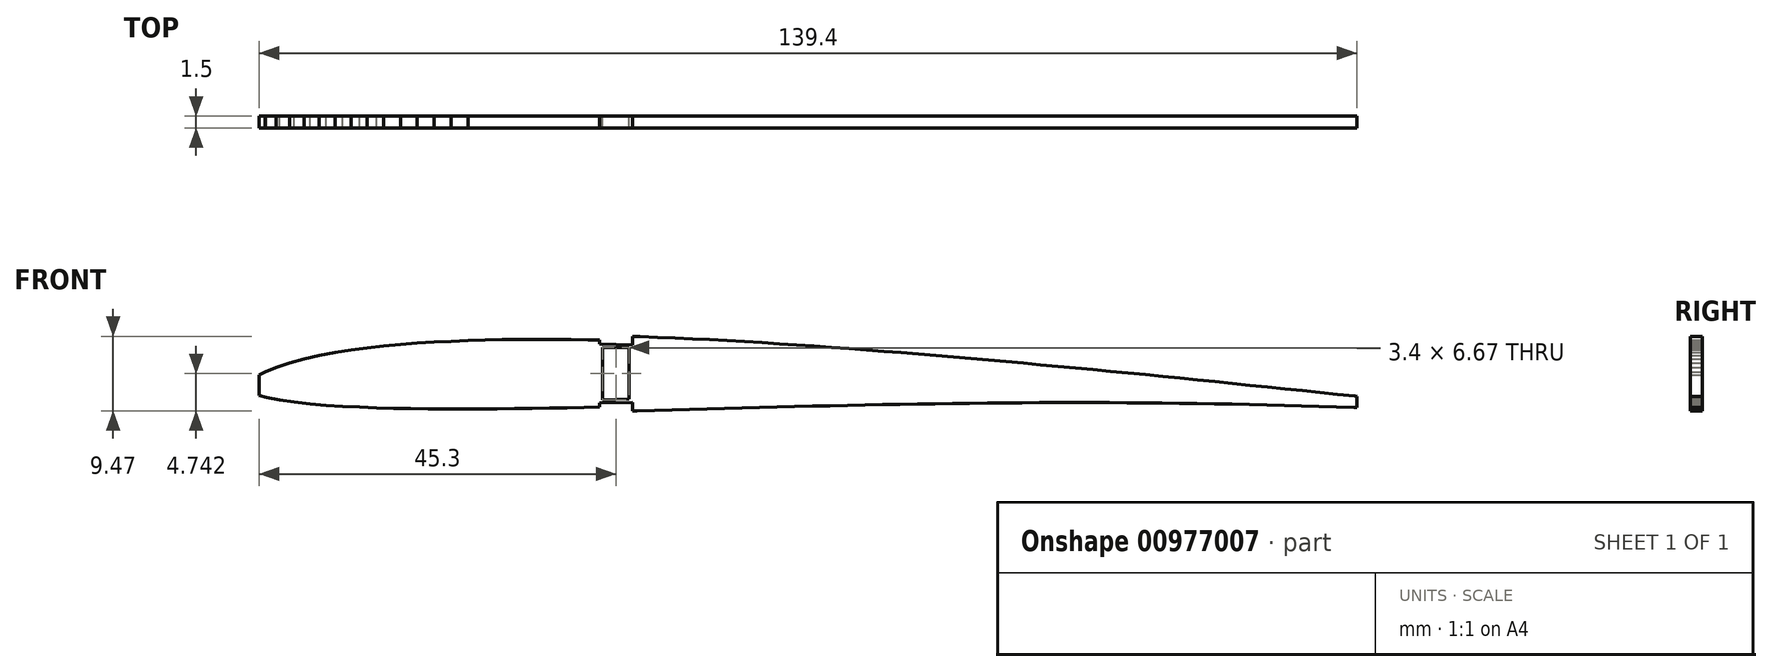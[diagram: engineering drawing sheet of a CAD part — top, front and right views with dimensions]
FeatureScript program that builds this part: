
annotation { "Feature Type Name" : "Feature", "Feature Type Description" : "" }
export const myFeature = defineFeature(function(context is Context, id is Id, definition is map)
    precondition{}
    {
        {
            var Q0;
            Q0=qCreatedBy(makeId("Front.planeOp"),FACE);
            var sketch = newSketch(context, id + "F0", { "sketchPlane" : qUnion([Q0])});
            skLineSegment(sketch, "E0", {"start": v(142, 2.16) * mm, "end": v(141.76, 2.2) * mm});
            skLineSegment(sketch, "E1", {"start": v(141.76, 2.2) * mm, "end": v(139.54, 2.42) * mm});
            skLineSegment(sketch, "E2", {"start": v(139.54, 2.42) * mm, "end": v(137.32, 2.66) * mm});
            skLineSegment(sketch, "E3", {"start": v(137.32, 2.66) * mm, "end": v(135.1, 2.89) * mm});
            skLineSegment(sketch, "E4", {"start": v(135.1, 2.89) * mm, "end": v(132.89, 3.12) * mm});
            skLineSegment(sketch, "E5", {"start": v(132.89, 3.12) * mm, "end": v(130.67, 3.35) * mm});
            skLineSegment(sketch, "E6", {"start": v(130.67, 3.35) * mm, "end": v(128.45, 3.57) * mm});
            skLineSegment(sketch, "E7", {"start": v(128.45, 3.57) * mm, "end": v(126.23, 3.8) * mm});
            skLineSegment(sketch, "E8", {"start": v(126.23, 3.8) * mm, "end": v(124.02, 4.03) * mm});
            skLineSegment(sketch, "E9", {"start": v(124.02, 4.03) * mm, "end": v(121.8, 4.25) * mm});
            skLineSegment(sketch, "E10", {"start": v(121.8, 4.25) * mm, "end": v(119.58, 4.47) * mm});
            skLineSegment(sketch, "E11", {"start": v(119.58, 4.47) * mm, "end": v(117.37, 4.7) * mm});
            skLineSegment(sketch, "E12", {"start": v(117.37, 4.7) * mm, "end": v(115.15, 4.91) * mm});
            skLineSegment(sketch, "E13", {"start": v(115.15, 4.91) * mm, "end": v(112.94, 5.13) * mm});
            skLineSegment(sketch, "E14", {"start": v(112.94, 5.13) * mm, "end": v(110.72, 5.34) * mm});
            skLineSegment(sketch, "E15", {"start": v(110.72, 5.34) * mm, "end": v(108.5, 5.56) * mm});
            skLineSegment(sketch, "E16", {"start": v(108.5, 5.56) * mm, "end": v(106.29, 5.77) * mm});
            skLineSegment(sketch, "E17", {"start": v(106.29, 5.77) * mm, "end": v(104.07, 5.98) * mm});
            skLineSegment(sketch, "E18", {"start": v(104.07, 5.98) * mm, "end": v(101.86, 6.18) * mm});
            skLineSegment(sketch, "E19", {"start": v(101.86, 6.18) * mm, "end": v(99.64, 6.38) * mm});
            skLineSegment(sketch, "E20", {"start": v(99.64, 6.38) * mm, "end": v(97.43, 6.58) * mm});
            skLineSegment(sketch, "E21", {"start": v(97.43, 6.58) * mm, "end": v(95.22, 6.78) * mm});
            skLineSegment(sketch, "E22", {"start": v(95.22, 6.78) * mm, "end": v(93, 6.98) * mm});
            skLineSegment(sketch, "E23", {"start": v(93, 6.98) * mm, "end": v(90.79, 7.17) * mm});
            skLineSegment(sketch, "E24", {"start": v(90.79, 7.17) * mm, "end": v(88.57, 7.35) * mm});
            skLineSegment(sketch, "E25", {"start": v(88.57, 7.35) * mm, "end": v(86.36, 7.54) * mm});
            skLineSegment(sketch, "E26", {"start": v(86.36, 7.54) * mm, "end": v(84.14, 7.72) * mm});
            skLineSegment(sketch, "E27", {"start": v(84.14, 7.72) * mm, "end": v(81.93, 7.9) * mm});
            skLineSegment(sketch, "E28", {"start": v(81.93, 7.9) * mm, "end": v(79.72, 8.06) * mm});
            skLineSegment(sketch, "E29", {"start": v(79.72, 8.06) * mm, "end": v(77.5, 8.23) * mm});
            skLineSegment(sketch, "E30", {"start": v(77.5, 8.23) * mm, "end": v(75.3, 8.4) * mm});
            skLineSegment(sketch, "E31", {"start": v(75.3, 8.4) * mm, "end": v(73.08, 8.55) * mm});
            skLineSegment(sketch, "E32", {"start": v(73.08, 8.55) * mm, "end": v(70.87, 8.7) * mm});
            skLineSegment(sketch, "E33", {"start": v(70.87, 8.7) * mm, "end": v(68.66, 8.85) * mm});
            skLineSegment(sketch, "E34", {"start": v(68.66, 8.85) * mm, "end": v(66.45, 8.98) * mm});
            skLineSegment(sketch, "E35", {"start": v(66.45, 8.98) * mm, "end": v(64.24, 9.12) * mm});
            skLineSegment(sketch, "E36", {"start": v(64.24, 9.12) * mm, "end": v(62.03, 9.24) * mm});
            skLineSegment(sketch, "E37", {"start": v(62.03, 9.24) * mm, "end": v(59.82, 9.36) * mm});
            skLineSegment(sketch, "E38", {"start": v(59.82, 9.36) * mm, "end": v(57.61, 9.47) * mm});
            skLineSegment(sketch, "E39", {"start": v(57.61, 9.47) * mm, "end": v(55.4, 9.57) * mm});
            skLineSegment(sketch, "E40", {"start": v(55.4, 9.57) * mm, "end": v(53.2, 9.66) * mm});
            skLineSegment(sketch, "E41", {"start": v(53.2, 9.66) * mm, "end": v(51, 9.74) * mm});
            skLineSegment(sketch, "E42", {"start": v(51, 9.74) * mm, "end": v(50, 9.78) * mm});
            skLineSegment(sketch, "E43", {"start": v(45.8, 9.3) * mm, "end": v(44.39, 9.33) * mm});
            skLineSegment(sketch, "E44", {"start": v(44.39, 9.33) * mm, "end": v(42.2, 9.36) * mm});
            skLineSegment(sketch, "E45", {"start": v(42.2, 9.36) * mm, "end": v(40, 9.39) * mm});
            skLineSegment(sketch, "E46", {"start": v(40, 9.39) * mm, "end": v(37.82, 9.4) * mm});
            skLineSegment(sketch, "E47", {"start": v(37.82, 9.4) * mm, "end": v(35.64, 9.39) * mm});
            skLineSegment(sketch, "E48", {"start": v(35.64, 9.39) * mm, "end": v(33.46, 9.36) * mm});
            skLineSegment(sketch, "E49", {"start": v(33.46, 9.36) * mm, "end": v(31.29, 9.32) * mm});
            skLineSegment(sketch, "E50", {"start": v(31.29, 9.32) * mm, "end": v(29.12, 9.25) * mm});
            skLineSegment(sketch, "E51", {"start": v(29.12, 9.25) * mm, "end": v(26.96, 9.16) * mm});
            skLineSegment(sketch, "E52", {"start": v(26.96, 9.16) * mm, "end": v(24.8, 9.05) * mm});
            skLineSegment(sketch, "E53", {"start": v(24.8, 9.05) * mm, "end": v(22.67, 8.92) * mm});
            skLineSegment(sketch, "E54", {"start": v(22.67, 8.92) * mm, "end": v(20.54, 8.75) * mm});
            skLineSegment(sketch, "E55", {"start": v(20.54, 8.75) * mm, "end": v(18.42, 8.55) * mm});
            skLineSegment(sketch, "E56", {"start": v(18.42, 8.55) * mm, "end": v(16.33, 8.32) * mm});
            skLineSegment(sketch, "E57", {"start": v(16.33, 8.32) * mm, "end": v(14.26, 8.04) * mm});
            skLineSegment(sketch, "E58", {"start": v(14.26, 8.04) * mm, "end": v(12.22, 7.72) * mm});
            skLineSegment(sketch, "E59", {"start": v(12.22, 7.72) * mm, "end": v(10.23, 7.35) * mm});
            skLineSegment(sketch, "E60", {"start": v(10.23, 7.35) * mm, "end": v(8.3, 6.91) * mm});
            skLineSegment(sketch, "E61", {"start": v(8.3, 6.91) * mm, "end": v(6.46, 6.42) * mm});
            skLineSegment(sketch, "E62", {"start": v(6.46, 6.42) * mm, "end": v(4.77, 5.86) * mm});
            skLineSegment(sketch, "E63", {"start": v(4.77, 5.86) * mm, "end": v(3.34, 5.26) * mm});
            skLineSegment(sketch, "E64", {"start": v(3.34, 5.26) * mm, "end": v(2.6, 4.87) * mm});
            skLineSegment(sketch, "E65", {"start": v(50, 9.78) * mm, "end": v(50, 9.18) * mm});
            skLineSegment(sketch, "E66", {"start": v(142, 0.74) * mm, "end": v(142, 2.16) * mm});
            skLineSegment(sketch, "E67", {"start": v(2.6, 2.28) * mm, "end": v(2.6, 4.87) * mm});
            skLineSegment(sketch, "E68", {"start": v(2.6, 2.28) * mm, "end": v(3.55, 2.03) * mm});
            skLineSegment(sketch, "E69", {"start": v(3.55, 2.03) * mm, "end": v(5.16, 1.7) * mm});
            skLineSegment(sketch, "E70", {"start": v(5.16, 1.7) * mm, "end": v(7.04, 1.43) * mm});
            skLineSegment(sketch, "E71", {"start": v(7.04, 1.43) * mm, "end": v(9.04, 1.2) * mm});
            skLineSegment(sketch, "E72", {"start": v(9.04, 1.2) * mm, "end": v(11.11, 1.03) * mm});
            skLineSegment(sketch, "E73", {"start": v(11.11, 1.03) * mm, "end": v(13.22, 0.9) * mm});
            skLineSegment(sketch, "E74", {"start": v(13.22, 0.9) * mm, "end": v(15.35, 0.79) * mm});
            skLineSegment(sketch, "E75", {"start": v(15.35, 0.79) * mm, "end": v(17.5, 0.7) * mm});
            skLineSegment(sketch, "E76", {"start": v(17.5, 0.7) * mm, "end": v(19.68, 0.64) * mm});
            skLineSegment(sketch, "E77", {"start": v(19.68, 0.64) * mm, "end": v(21.86, 0.6) * mm});
            skLineSegment(sketch, "E78", {"start": v(21.86, 0.6) * mm, "end": v(24.04, 0.57) * mm});
            skLineSegment(sketch, "E79", {"start": v(24.04, 0.57) * mm, "end": v(26.23, 0.56) * mm});
            skLineSegment(sketch, "E80", {"start": v(26.23, 0.56) * mm, "end": v(28.43, 0.56) * mm});
            skLineSegment(sketch, "E81", {"start": v(28.43, 0.56) * mm, "end": v(30.63, 0.56) * mm});
            skLineSegment(sketch, "E82", {"start": v(30.63, 0.56) * mm, "end": v(32.83, 0.58) * mm});
            skLineSegment(sketch, "E83", {"start": v(32.83, 0.58) * mm, "end": v(35.04, 0.6) * mm});
            skLineSegment(sketch, "E84", {"start": v(35.04, 0.6) * mm, "end": v(37.25, 0.64) * mm});
            skLineSegment(sketch, "E85", {"start": v(37.25, 0.64) * mm, "end": v(39.46, 0.67) * mm});
            skLineSegment(sketch, "E86", {"start": v(39.46, 0.67) * mm, "end": v(41.67, 0.72) * mm});
            skLineSegment(sketch, "E87", {"start": v(41.67, 0.72) * mm, "end": v(43.9, 0.77) * mm});
            skLineSegment(sketch, "E88", {"start": v(43.9, 0.77) * mm, "end": v(45.8, 0.8) * mm});
            skLineSegment(sketch, "E89", {"start": v(50, 0.31) * mm, "end": v(50.57, 0.33) * mm});
            skLineSegment(sketch, "E90", {"start": v(50.57, 0.33) * mm, "end": v(52.8, 0.38) * mm});
            skLineSegment(sketch, "E91", {"start": v(52.8, 0.38) * mm, "end": v(55.02, 0.44) * mm});
            skLineSegment(sketch, "E92", {"start": v(55.02, 0.44) * mm, "end": v(57.25, 0.5) * mm});
            skLineSegment(sketch, "E93", {"start": v(57.25, 0.5) * mm, "end": v(59.48, 0.56) * mm});
            skLineSegment(sketch, "E94", {"start": v(59.48, 0.56) * mm, "end": v(61.7, 0.62) * mm});
            skLineSegment(sketch, "E95", {"start": v(61.7, 0.62) * mm, "end": v(63.94, 0.68) * mm});
            skLineSegment(sketch, "E96", {"start": v(63.94, 0.68) * mm, "end": v(66.17, 0.74) * mm});
            skLineSegment(sketch, "E97", {"start": v(66.17, 0.74) * mm, "end": v(68.4, 0.8) * mm});
            skLineSegment(sketch, "E98", {"start": v(68.4, 0.8) * mm, "end": v(70.62, 0.86) * mm});
            skLineSegment(sketch, "E99", {"start": v(70.62, 0.86) * mm, "end": v(72.85, 0.91) * mm});
            skLineSegment(sketch, "E100", {"start": v(72.85, 0.91) * mm, "end": v(75.07, 0.97) * mm});
            skLineSegment(sketch, "E101", {"start": v(75.07, 0.97) * mm, "end": v(77.3, 1.02) * mm});
            skLineSegment(sketch, "E102", {"start": v(77.3, 1.02) * mm, "end": v(79.52, 1.06) * mm});
            skLineSegment(sketch, "E103", {"start": v(79.52, 1.06) * mm, "end": v(81.74, 1.1) * mm});
            skLineSegment(sketch, "E104", {"start": v(81.74, 1.1) * mm, "end": v(83.97, 1.15) * mm});
            skLineSegment(sketch, "E105", {"start": v(83.97, 1.15) * mm, "end": v(86.19, 1.2) * mm});
            skLineSegment(sketch, "E106", {"start": v(86.19, 1.2) * mm, "end": v(88.41, 1.23) * mm});
            skLineSegment(sketch, "E107", {"start": v(88.41, 1.23) * mm, "end": v(90.63, 1.26) * mm});
            skLineSegment(sketch, "E108", {"start": v(90.63, 1.26) * mm, "end": v(92.85, 1.29) * mm});
            skLineSegment(sketch, "E109", {"start": v(92.85, 1.29) * mm, "end": v(95.07, 1.31) * mm});
            skLineSegment(sketch, "E110", {"start": v(95.07, 1.31) * mm, "end": v(97.3, 1.33) * mm});
            skLineSegment(sketch, "E111", {"start": v(97.3, 1.33) * mm, "end": v(99.51, 1.35) * mm});
            skLineSegment(sketch, "E112", {"start": v(99.51, 1.35) * mm, "end": v(101.73, 1.36) * mm});
            skLineSegment(sketch, "E113", {"start": v(101.73, 1.36) * mm, "end": v(103.95, 1.36) * mm});
            skLineSegment(sketch, "E114", {"start": v(103.95, 1.36) * mm, "end": v(106.17, 1.37) * mm});
            skLineSegment(sketch, "E115", {"start": v(106.17, 1.37) * mm, "end": v(108.4, 1.36) * mm});
            skLineSegment(sketch, "E116", {"start": v(108.4, 1.36) * mm, "end": v(110.61, 1.36) * mm});
            skLineSegment(sketch, "E117", {"start": v(110.61, 1.36) * mm, "end": v(112.83, 1.34) * mm});
            skLineSegment(sketch, "E118", {"start": v(112.83, 1.34) * mm, "end": v(115.05, 1.33) * mm});
            skLineSegment(sketch, "E119", {"start": v(115.05, 1.33) * mm, "end": v(117.27, 1.3) * mm});
            skLineSegment(sketch, "E120", {"start": v(117.27, 1.3) * mm, "end": v(119.48, 1.28) * mm});
            skLineSegment(sketch, "E121", {"start": v(119.48, 1.28) * mm, "end": v(121.7, 1.25) * mm});
            skLineSegment(sketch, "E122", {"start": v(121.7, 1.25) * mm, "end": v(123.92, 1.21) * mm});
            skLineSegment(sketch, "E123", {"start": v(123.92, 1.21) * mm, "end": v(126.14, 1.17) * mm});
            skLineSegment(sketch, "E124", {"start": v(126.14, 1.17) * mm, "end": v(128.36, 1.13) * mm});
            skLineSegment(sketch, "E125", {"start": v(128.36, 1.13) * mm, "end": v(130.57, 1.08) * mm});
            skLineSegment(sketch, "E126", {"start": v(130.57, 1.08) * mm, "end": v(132.8, 1.02) * mm});
            skLineSegment(sketch, "E127", {"start": v(132.8, 1.02) * mm, "end": v(135, 0.96) * mm});
            skLineSegment(sketch, "E128", {"start": v(135, 0.96) * mm, "end": v(137.23, 0.9) * mm});
            skLineSegment(sketch, "E129", {"start": v(137.23, 0.9) * mm, "end": v(139.45, 0.83) * mm});
            skLineSegment(sketch, "E130", {"start": v(139.45, 0.83) * mm, "end": v(141.66, 0.76) * mm});
            skLineSegment(sketch, "E131", {"start": v(141.66, 0.76) * mm, "end": v(142, 0.74) * mm});
            skLineSegment(sketch, "E132", {"start": v(50, 0.91) * mm, "end": v(50, 0.31) * mm});
            skLineSegment(sketch, "E133", {"start": v(45.8, 8.8) * mm, "end": v(50, 8.68) * mm});
            skLineSegment(sketch, "E134", {"start": v(45.8, 1.3) * mm, "end": v(50, 1.41) * mm});
            skLineSegment(sketch, "E135", {"start": v(50, 9.18) * mm, "end": v(50, 8.68) * mm});
            skLineSegment(sketch, "E136", {"start": v(50, 1.41) * mm, "end": v(50, 0.91) * mm});
            skLineSegment(sketch, "E137", {"start": v(45.8, 9.3) * mm, "end": v(45.8, 8.8) * mm});
            skLineSegment(sketch, "E138", {"start": v(45.8, 1.3) * mm, "end": v(45.8, 0.8) * mm});
            skLineSegment(sketch, "E139", {"start": v(46.2, 8.39) * mm, "end": v(49.6, 8.29) * mm});
            skLineSegment(sketch, "E140", {"start": v(46.2, 1.72) * mm, "end": v(49.6, 1.8) * mm});
            skLineSegment(sketch, "E141", {"start": v(46.2, 8.39) * mm, "end": v(46.2, 1.72) * mm});
            skLineSegment(sketch, "E142", {"start": v(49.6, 8.29) * mm, "end": v(49.6, 1.8) * mm});
            skSolve(sketch);
        }
        {
            var Q0;
            Q0=makeQuery(id+"F0.imprint","IMPRINT",FACE,{"disambiguationData":[TD([[makeQuery(id+"F0.imprint","IMPRINT",EDGE,{"derivedFrom":sQuery(id+"F0.wireOp",EDGE,"E0")}),1.0]])]});
            extrude(context, id + "F1", {"entities" : qUnion([Q0]), "depth" : 1.5 * mm, "offsetDistance" : 25.4 * mm});
        }
    });
